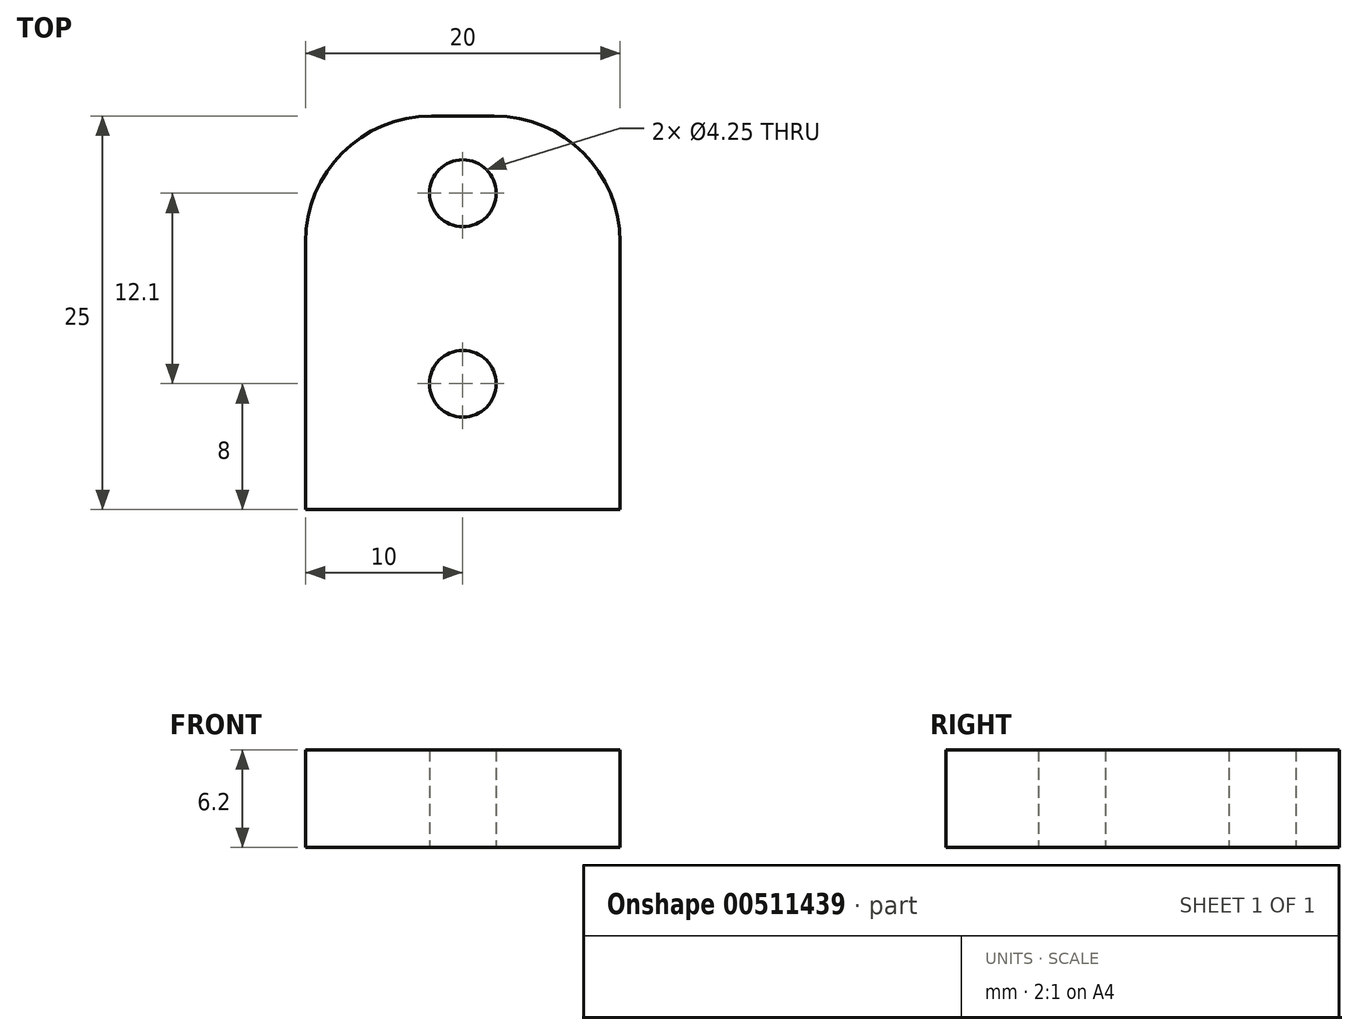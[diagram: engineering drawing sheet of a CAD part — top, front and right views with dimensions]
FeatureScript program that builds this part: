
annotation { "Feature Type Name" : "Feature", "Feature Type Description" : "" }
export const myFeature = defineFeature(function(context is Context, id is Id, definition is map)
    precondition{}
    {
        {
            var Q0;
            Q0=qCreatedBy(makeId("Top.planeOp"),FACE);
            var sketch = newSketch(context, id + "F0", { "sketchPlane" : qUnion([Q0])});
            skLineSegment(sketch, "E0.bottom", {"start": v(10, 12.5) * mm, "end": v(-10, 12.5) * mm});
            skLineSegment(sketch, "E0.top", {"start": v(10, -12.5) * mm, "end": v(-10, -12.5) * mm});
            skLineSegment(sketch, "E0.left", {"start": v(10, 12.5) * mm, "end": v(10, -12.5) * mm});
            skLineSegment(sketch, "E0.right", {"start": v(-10, 12.5) * mm, "end": v(-10, -12.5) * mm});
            skPoint(sketch, "E0.middle", {"position": v(0, 0) * mm});
            skLineSegment(sketch, "E1", {"start": v(0, -12.5) * mm, "end": v(0, -4.5) * mm, "construction": true});
            skLineSegment(sketch, "E2", {"start": v(0, -4.5) * mm, "end": v(0, 7.6) * mm, "construction": true});
            skCircle(sketch, "E3", {"center": v(0, 7.6) * mm, "radius": 2.12 * mm});
            skCircle(sketch, "E4", {"center": v(0, -4.5) * mm, "radius": 2.12 * mm});
            skSolve(sketch);
        }
        {
            var Q0;
            Q0=makeQuery(id+"F0.imprint","IMPRINT",FACE,{"disambiguationData":[TD([[makeQuery(id+"F0.imprint","IMPRINT",EDGE,{"derivedFrom":sQuery(id+"F0.wireOp",EDGE,"E0.bottom")}),1.0]])]});
            extrude(context, id + "F1", {"entities" : qUnion([Q0]), "depth" : 6.2 * mm, "offsetDistance" : 25 * mm});
        }
        {
            var Q0;
            Q0=makeQuery(id+"F1.opExtrude","SWEPT_EDGE",EDGE,{"disambiguationData":[OSD([sQuery(id+"F0.wireOp",EDGE,"E0.bottom"),sQuery(id+"F0.wireOp",EDGE,"E0.right")])]});
            var Q1;
            Q1=makeQuery(id+"F1.opExtrude","SWEPT_EDGE",EDGE,{"disambiguationData":[OSD([sQuery(id+"F0.wireOp",EDGE,"E0.bottom"),sQuery(id+"F0.wireOp",EDGE,"E0.left")])]});
            fillet(context, id + "F2", {"entities" : qUnion([Q0, Q1]), "radius" : 8 * mm, "tangentPropagation" : true, "allowEdgeOverflow" : false});
        }
    });
